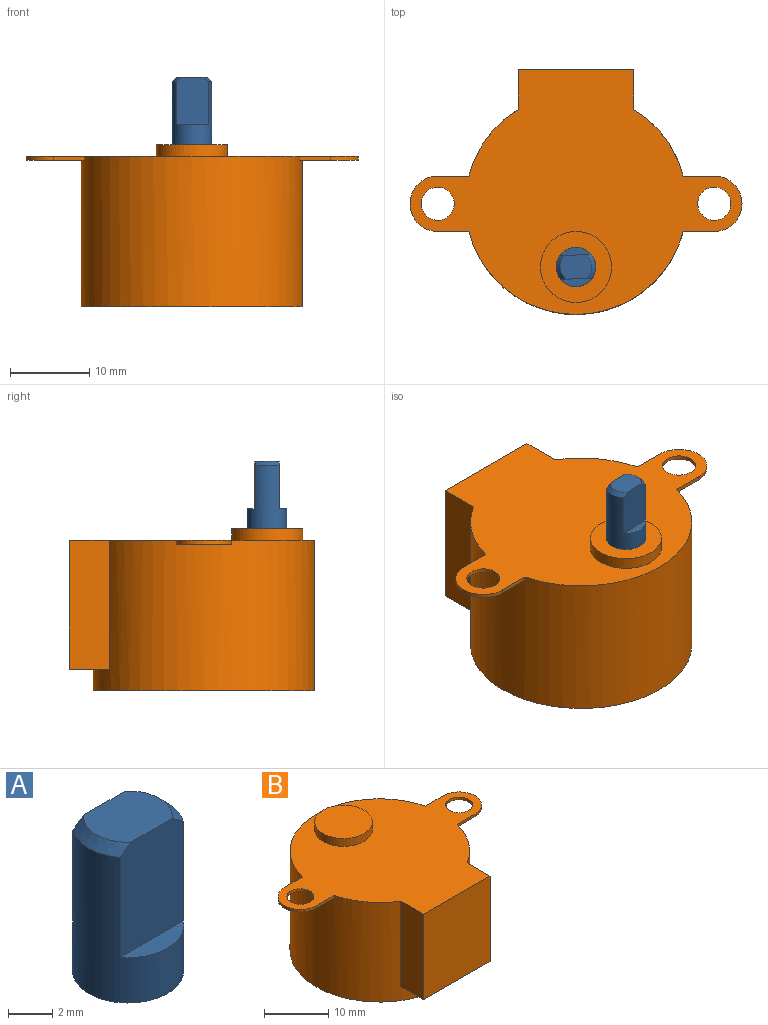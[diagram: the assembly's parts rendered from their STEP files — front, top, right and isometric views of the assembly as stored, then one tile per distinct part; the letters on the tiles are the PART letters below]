
ASSEMBLY  parts=2 mates=1
PART A: 9 faces, bbox 5x5x8.5 mm
  f0: plane 4x1mm, normal (0,0,1), area 2.8mm2, adj f2,f4
  f1: plane 4x1mm, normal (0,0,1), area 2.8mm2, adj f2,f5
  f2: cylinder r=2.5mm len=8mm, axis (0,0,-1), area 74.7mm2, adj f0,f1,f3,f4,f5,f7,f8
  f3: plane 5x5mm, normal (0,0,-1), area 19.6mm2, adj f2
  f4: plane 6x4mm, normal (0,1,0), area 23.7mm2, adj f0,f2,f6,f7,f8
  f5: plane 6x4mm, normal (0,-1,0), area 23.7mm2, adj f1,f2,f6,f7,f8
  f6: plane 4x3mm, normal (0,0,1), area 10.8mm2, adj f4,f5,f7,f8
  f7: cone r=2mm half-angle=45deg, axis (0,0,-1), area 2.3mm2, adj f2,f4,f5,f6
  f8: cone r=2mm half-angle=45deg, axis (0,0,-1), area 2.3mm2, adj f2,f4,f5,f6
PART B: 19 faces, bbox 42x31x20.5 mm
  f0: cylinder r=14mm len=28mm, axis (0,0,1), area 1413.9mm2, adj f1,f2,f7,f8,f9,f10,f11,f13
  f1: plane 28x28mm, normal (0,0,-1), area 615.8mm2, adj f0
  f2: plane 42x31mm, normal (0,0,1), area 667.5mm2, adj f0,f3,f5,f6,f8,f9,f11,f12
  f3: cylinder r=4.5mm len=9mm, axis (0,0,-1), area 42.4mm2, adj f2,f4
  f4: plane 9x9mm, normal (0,0,1), area 63.6mm2, adj f3
  f5: cylinder r=2.1mm len=4.2mm, axis (0,0,1), area 6.6mm2, adj f2,f7
  f6: cylinder r=3.5mm len=7mm, axis (0,0,1), area 5.5mm2, adj f2,f7,f8,f9
  f7: plane 7.44x7mm, normal (0,0,-1), area 30.9mm2, adj f0,f5,f6,f8,f9
  f8: plane 3.94x0.5mm, normal (0,-1,0), area 2mm2, adj f0,f2,f6,f7
  f9: plane 3.94x0.5mm, normal (0,1,0), area 2mm2, adj f0,f2,f6,f7
  f10: plane 7.44x7mm, normal (0,0,-1), area 30.9mm2, adj f0,f11,f12,f13,f14
  f11: plane 3.94x0.5mm, normal (0,1,0), area 2mm2, adj f0,f2,f10,f12
  f12: cylinder r=3.5mm len=7mm, axis (0,0,1), area 5.5mm2, adj f2,f10,f11,f13
  f13: plane 3.94x0.5mm, normal (0,-1,0), area 2mm2, adj f0,f2,f10,f12
  f14: cylinder r=2.1mm len=4.2mm, axis (0,0,1), area 6.6mm2, adj f2,f10
  f15: plane 14.6x5.05mm, normal (0,0,-1), area 53.5mm2, adj f0,f16,f17,f18
  f16: plane 16.3x5.05mm, normal (1,0,0), area 82.4mm2, adj f0,f2,f15,f18
  f17: plane 16.3x5.05mm, normal (-1,0,0), area 82.4mm2, adj f0,f2,f15,f18
  f18: plane 16.3x14.6mm, normal (0,-1,0), area 238mm2, adj f2,f15,f16,f17
PLACE A rot(axis=(0,0,-1),177.5deg) t=(5.01,23.75,27.28)mm
PLACE B rot(axis=(0,0,-1),180deg) t=(5.01,31.75,25.78)mm fixed
MATE revolute B.f3 <-> A.f2  axis (0,0,1) through (5.01,23.75,27.28)mm
